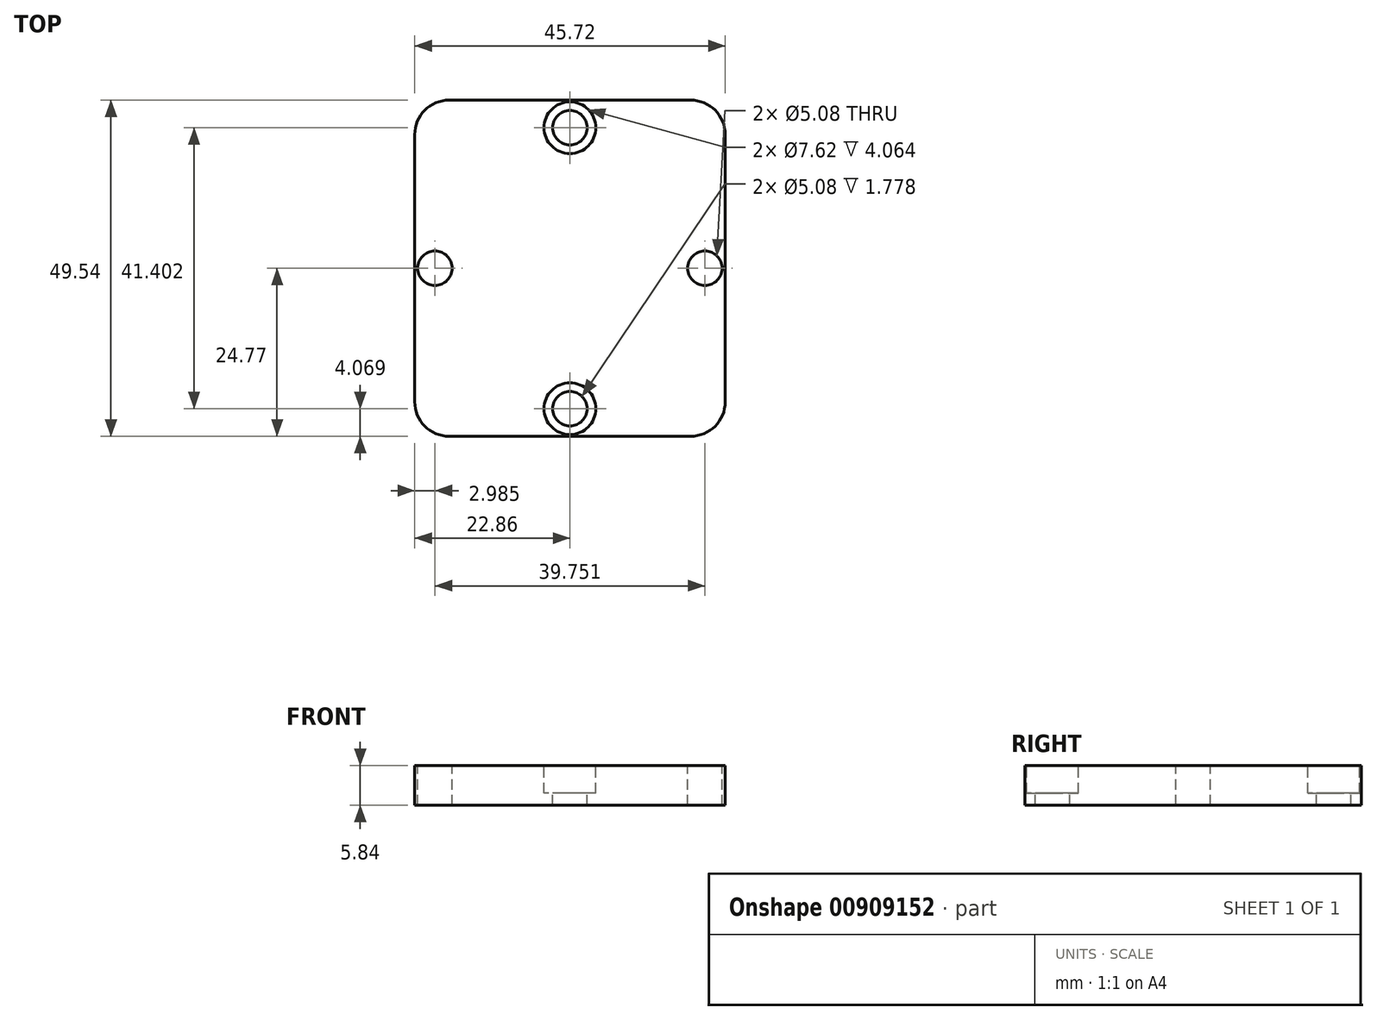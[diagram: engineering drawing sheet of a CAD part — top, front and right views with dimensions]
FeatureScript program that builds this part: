
annotation { "Feature Type Name" : "Feature", "Feature Type Description" : "" }
export const myFeature = defineFeature(function(context is Context, id is Id, definition is map)
    precondition{}
    {
        {
            var Q0;
            Q0=qCreatedBy(makeId("Top.planeOp"),FACE);
            var sketch = newSketch(context, id + "F0", { "sketchPlane" : qUnion([Q0])});
            skLineSegment(sketch, "E0.bottom", {"start": v(-22.86, 24.77) * mm, "end": v(22.86, 24.77) * mm});
            skLineSegment(sketch, "E0.top", {"start": v(-22.86, -24.77) * mm, "end": v(22.86, -24.77) * mm});
            skLineSegment(sketch, "E0.left", {"start": v(-22.86, 24.77) * mm, "end": v(-22.86, -24.77) * mm});
            skLineSegment(sketch, "E0.right", {"start": v(22.86, 24.77) * mm, "end": v(22.86, -24.77) * mm});
            skSolve(sketch);
        }
        {
            var Q0;
            Q0=makeQuery(id+"F0.imprint","IMPRINT",FACE,{"disambiguationData":[TD([[makeQuery(id+"F0.imprint","IMPRINT",EDGE,{"derivedFrom":sQuery(id+"F0.wireOp",EDGE,"E0.bottom")}),-1.0]])]});
            var Q1;
            Q1 = qSketchRegion(id + "F2", true);
            extrude(context, id + "F1", {"entities" : qUnion([Q0, Q1]), "depth" : 5.84 * mm, "offsetDistance" : 25.4 * mm});
        }
        {
            var Q0;
            Q0=makeQuery(id+"F1.opExtrude","CAP_FACE",FACE,{"disambiguationData":[OSD([sQuery(id+"F0.wireOp",EDGE,"E0.bottom"),sQuery(id+"F0.wireOp",EDGE,"E0.top"),sQuery(id+"F0.wireOp",EDGE,"E0.left"),sQuery(id+"F0.wireOp",EDGE,"E0.right")])],"isStart":false});
            var sketch = newSketch(context, id + "F2", { "sketchPlane" : qUnion([Q0])});
            skCircle(sketch, "E1", {"center": v(-19.88, 0) * mm, "radius": 2.54 * mm});
            skCircle(sketch, "E2", {"center": v(19.88, 0) * mm, "radius": 2.54 * mm});
            skSolve(sketch);
        }
        {
            var Q0;
            Q0=makeQuery(id+"F2.imprint","IMPRINT",FACE,{"disambiguationData":[TD([[makeQuery(id+"F2.imprint","IMPRINT",EDGE,{"derivedFrom":sQuery(id+"F2.wireOp",EDGE,"E1")}),1.0]])]});
            var Q1;
            Q1=makeQuery(id+"F2.imprint","IMPRINT",FACE,{"disambiguationData":[TD([[makeQuery(id+"F2.imprint","IMPRINT",EDGE,{"derivedFrom":sQuery(id+"F2.wireOp",EDGE,"E2")}),1.0]])]});
            extrude(context, id + "F3", {"entities" : qUnion([Q0, Q1]), "operationType" : NewBodyOperationType.REMOVE, "oppositeDirection" : true, "depth" : 25.4 * mm, "offsetDistance" : 25.4 * mm});
        }
        {
            var Q0;
            Q0=makeQuery(id+"F1.opExtrude","CAP_FACE",FACE,{"disambiguationData":[OSD([sQuery(id+"F0.wireOp",EDGE,"E0.bottom"),sQuery(id+"F0.wireOp",EDGE,"E0.top"),sQuery(id+"F0.wireOp",EDGE,"E0.left"),sQuery(id+"F0.wireOp",EDGE,"E0.right")])],"isStart":false});
            var sketch = newSketch(context, id + "F4", { "sketchPlane" : qUnion([Q0])});
            skCircle(sketch, "E3", {"center": v(0, 20.7) * mm, "radius": 3.81 * mm});
            skCircle(sketch, "E4", {"center": v(0, -20.7) * mm, "radius": 3.81 * mm});
            skSolve(sketch);
        }
        {
            var Q0;
            Q0=makeQuery(id+"F4.imprint","IMPRINT",FACE,{"disambiguationData":[TD([[makeQuery(id+"F4.imprint","IMPRINT",EDGE,{"derivedFrom":sQuery(id+"F4.wireOp",EDGE,"E3")}),1.0]])]});
            var Q1;
            Q1=makeQuery(id+"F4.imprint","IMPRINT",FACE,{"disambiguationData":[TD([[makeQuery(id+"F4.imprint","IMPRINT",EDGE,{"derivedFrom":sQuery(id+"F4.wireOp",EDGE,"E4")}),1.0]])]});
            extrude(context, id + "F5", {"entities" : qUnion([Q0, Q1]), "operationType" : NewBodyOperationType.REMOVE, "oppositeDirection" : true, "depth" : 4.06 * mm, "offsetDistance" : 25.4 * mm});
        }
        {
            var Q0;
            Q0=makeQuery(id+"F1.opExtrude","CAP_FACE",FACE,{"disambiguationData":[OSD([sQuery(id+"F0.wireOp",EDGE,"E0.bottom"),sQuery(id+"F0.wireOp",EDGE,"E0.top"),sQuery(id+"F0.wireOp",EDGE,"E0.left"),sQuery(id+"F0.wireOp",EDGE,"E0.right")])],"isStart":false});
            var sketch = newSketch(context, id + "F6", { "sketchPlane" : qUnion([Q0])});
            skCircle(sketch, "E5", {"center": v(0, 20.7) * mm, "radius": 2.54 * mm});
            skCircle(sketch, "E6", {"center": v(0, -20.7) * mm, "radius": 2.54 * mm});
            skSolve(sketch);
        }
        {
            var Q0;
            Q0=makeQuery(id+"F6.imprint","IMPRINT",FACE,{"disambiguationData":[TD([[makeQuery(id+"F6.imprint","IMPRINT",EDGE,{"derivedFrom":sQuery(id+"F6.wireOp",EDGE,"E5")}),1.0]])]});
            var Q1;
            Q1=makeQuery(id+"F6.imprint","IMPRINT",FACE,{"disambiguationData":[TD([[makeQuery(id+"F6.imprint","IMPRINT",EDGE,{"derivedFrom":sQuery(id+"F6.wireOp",EDGE,"E6")}),1.0]])]});
            extrude(context, id + "F7", {"entities" : qUnion([Q0, Q1]), "operationType" : NewBodyOperationType.REMOVE, "oppositeDirection" : true, "depth" : 25.4 * mm, "offsetDistance" : 25.4 * mm});
        }
        {
            var Q0;
            Q0=makeQuery(id+"F1.opExtrude","SWEPT_EDGE",EDGE,{"disambiguationData":[OSD([sQuery(id+"F0.wireOp",EDGE,"E0.bottom"),sQuery(id+"F0.wireOp",EDGE,"E0.left")])]});
            var Q1;
            Q1=makeQuery(id+"F1.opExtrude","SWEPT_EDGE",EDGE,{"disambiguationData":[OSD([sQuery(id+"F0.wireOp",EDGE,"E0.top"),sQuery(id+"F0.wireOp",EDGE,"E0.left")])]});
            var Q2;
            Q2=makeQuery(id+"F1.opExtrude","SWEPT_EDGE",EDGE,{"disambiguationData":[OSD([sQuery(id+"F0.wireOp",EDGE,"E0.top"),sQuery(id+"F0.wireOp",EDGE,"E0.right")])]});
            var Q3;
            Q3=makeQuery(id+"F1.opExtrude","SWEPT_EDGE",EDGE,{"disambiguationData":[OSD([sQuery(id+"F0.wireOp",EDGE,"E0.bottom"),sQuery(id+"F0.wireOp",EDGE,"E0.right")])]});
            fillet(context, id + "F8", {"entities" : qUnion([Q0, Q1, Q2, Q3]), "radius" : 5.08 * mm, "tangentPropagation" : true, "allowEdgeOverflow" : false});
        }
    });
